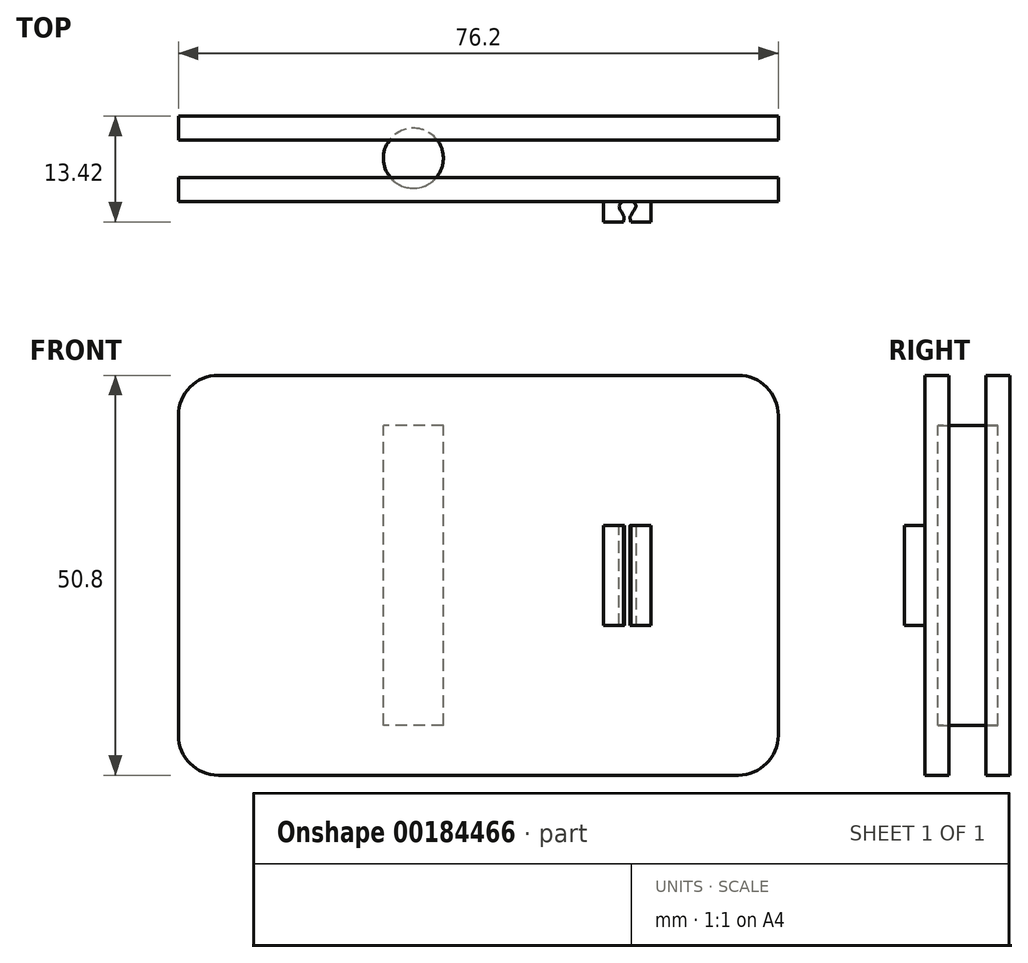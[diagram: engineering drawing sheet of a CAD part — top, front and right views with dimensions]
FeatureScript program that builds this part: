
annotation { "Feature Type Name" : "Feature", "Feature Type Description" : "" }
export const myFeature = defineFeature(function(context is Context, id is Id, definition is map)
    precondition{}
    {
        {
            var Q0;
            Q0=qCreatedBy(makeId("Front.planeOp"),FACE);
            var sketch = newSketch(context, id + "F0", { "sketchPlane" : qUnion([Q0])});
            skLineSegment(sketch, "E0.bottom", {"start": v(38.1, 25.4) * mm, "end": v(-38.1, 25.4) * mm});
            skLineSegment(sketch, "E0.top", {"start": v(38.1, -25.4) * mm, "end": v(-38.1, -25.4) * mm});
            skLineSegment(sketch, "E0.left", {"start": v(38.1, 25.4) * mm, "end": v(38.1, -25.4) * mm});
            skLineSegment(sketch, "E0.right", {"start": v(-38.1, 25.4) * mm, "end": v(-38.1, -25.4) * mm});
            skPoint(sketch, "E0.middle", {"position": v(0, 0) * mm});
            skSolve(sketch);
        }
        {
            var Q0;
            Q0=makeQuery(id+"F0.imprint","IMPRINT",FACE,{"disambiguationData":[TD([[makeQuery(id+"F0.imprint","IMPRINT",EDGE,{"derivedFrom":sQuery(id+"F0.wireOp",EDGE,"E0.bottom")}),1.0]])]});
            extrude(context, id + "F1", {"entities" : qUnion([Q0]), "depth" : 3.05 * mm});
        }
        {
            var Q0;
            Q0=qCreatedBy(makeId("Top.planeOp"),FACE);
            var sketch = newSketch(context, id + "F2", { "sketchPlane" : qUnion([Q0])});
            skPoint(sketch, "E1", {"position": v(-8.25, 2.43) * mm});
            skCircle(sketch, "E2", {"center": v(-8.25, 2.43) * mm, "radius": 3.8 * mm});
            skSolve(sketch);
        }
        {
            var Q0;
            Q0=makeQuery(id+"F2.imprint","IMPRINT",FACE,{"disambiguationData":[TD([[makeQuery(id+"F2.imprint","IMPRINT",EDGE,{"derivedFrom":sQuery(id+"F2.wireOp",EDGE,"E2")}),1.0]])]});
            extrude(context, id + "F3", {"entities" : qUnion([Q0]), "endBound" : BoundingType.SYMMETRIC, "oppositeDirection" : true, "depth" : 38.1 * mm});
        }
        {
            var Q0;
            Q0=qCreatedBy(makeId("Right.planeOp"),FACE);
            var sketch = newSketch(context, id + "F4", { "sketchPlane" : qUnion([Q0])});
            skLineSegment(sketch, "E3.bottom", {"start": v(4.71, -25.4) * mm, "end": v(7.76, -25.4) * mm});
            skLineSegment(sketch, "E3.top", {"start": v(4.71, 25.4) * mm, "end": v(7.76, 25.4) * mm});
            skLineSegment(sketch, "E3.left", {"start": v(4.71, -25.4) * mm, "end": v(4.71, 25.4) * mm});
            skLineSegment(sketch, "E3.right", {"start": v(7.76, -25.4) * mm, "end": v(7.76, 25.4) * mm});
            skPoint(sketch, "E3.middle", {"position": v(6.24, 0) * mm});
            skSolve(sketch);
        }
        {
            var Q0;
            Q0 = qSketchRegion(id + "F4", true);
            extrude(context, id + "F5", {"entities" : qUnion([Q0]), "endBound" : BoundingType.SYMMETRIC, "depth" : 76.2 * mm});
        }
        {
            var Q0;
            Q0=qCreatedBy(makeId("Top.planeOp"),FACE);
            var sketch = newSketch(context, id + "F6", { "sketchPlane" : qUnion([Q0])});
            skPoint(sketch, "E4", {"position": v(15.88, -2.87) * mm});
            skPoint(sketch, "E5", {"position": v(21.94, -2.87) * mm});
            skPoint(sketch, "E6", {"position": v(21.94, -3.6) * mm});
            skPoint(sketch, "E7", {"position": v(15.88, -3.6) * mm});
            skPoint(sketch, "E8", {"position": v(15.88, -4.77) * mm});
            skPoint(sketch, "E9", {"position": v(15.88, -5.66) * mm});
            skPoint(sketch, "E10", {"position": v(21.94, -4.77) * mm});
            skPoint(sketch, "E11", {"position": v(21.94, -5.66) * mm});
            skLineSegment(sketch, "E12", {"start": v(15.88, -5.66) * mm, "end": v(18.42, -5.66) * mm});
            skLineSegment(sketch, "E13", {"start": v(15.88, -5.66) * mm, "end": v(15.88, -2.87) * mm});
            skLineSegment(sketch, "E14", {"start": v(19.4, -5.66) * mm, "end": v(21.94, -5.66) * mm});
            skLineSegment(sketch, "E15", {"start": v(21.94, -2.87) * mm, "end": v(21.94, -5.66) * mm});
            skFitSpline(sketch, "E16", {"points": [v(15.88, -2.87) * mm, v(18.9, -1.91) * mm, v(21.94, -2.87) * mm], "startDerivative": vector(2.6, 1.29) * mm, "endDerivative": vector(2.6, -1.33) * mm});
            skFitSpline(sketch, "E17", {"points": [v(18.42, -5.66) * mm, v(18.42, -4.77) * mm, v(17.9, -3.6) * mm, v(19.05, -2.99) * mm, v(20, -3.6) * mm, v(19.4, -4.77) * mm, v(19.4, -5.66) * mm], "startDerivative": vector(2.47, 8.7) * mm, "endDerivative": vector(2.78, -8.49) * mm});
            skSolve(sketch);
        }
        {
            var Q0;
            Q0=makeQuery(id+"F6.imprint","IMPRINT",FACE,{"disambiguationData":[TD([[makeQuery(id+"F6.imprint","IMPRINT",EDGE,{"derivedFrom":sQuery(id+"F6.wireOp",EDGE,"E12")}),1.0]])]});
            extrude(context, id + "F7", {"entities" : qUnion([Q0]), "operationType" : NewBodyOperationType.ADD, "endBound" : BoundingType.SYMMETRIC, "depth" : 12.7 * mm});
        }
        {
            var Q0;
            Q0=makeQuery(id+"F1.opExtrude","SWEPT_EDGE",EDGE,{"disambiguationData":[OSD([sQuery(id+"F0.wireOp",EDGE,"E0.top"),sQuery(id+"F0.wireOp",EDGE,"E0.left")])]});
            var Q1;
            Q1=makeQuery(id+"F5.opExtrude","CAP_EDGE",EDGE,{"disambiguationData":[OSD([sQuery(id+"F4.wireOp",EDGE,"E3.bottom")])],"isStart":false});
            var Q2;
            Q2=makeQuery(id+"F1.opExtrude","SWEPT_EDGE",EDGE,{"disambiguationData":[OSD([sQuery(id+"F0.wireOp",EDGE,"E0.top"),sQuery(id+"F0.wireOp",EDGE,"E0.right")])]});
            var Q3;
            Q3=makeQuery(id+"F5.opExtrude","CAP_EDGE",EDGE,{"disambiguationData":[OSD([sQuery(id+"F4.wireOp",EDGE,"E3.bottom")])],"isStart":true});
            var Q4;
            Q4=makeQuery(id+"F1.opExtrude","SWEPT_EDGE",EDGE,{"disambiguationData":[OSD([sQuery(id+"F0.wireOp",EDGE,"E0.bottom"),sQuery(id+"F0.wireOp",EDGE,"E0.left")])]});
            var Q5;
            Q5=makeQuery(id+"F5.opExtrude","CAP_EDGE",EDGE,{"disambiguationData":[OSD([sQuery(id+"F4.wireOp",EDGE,"E3.top")])],"isStart":false});
            var Q6;
            Q6=makeQuery(id+"F1.opExtrude","SWEPT_EDGE",EDGE,{"disambiguationData":[OSD([sQuery(id+"F0.wireOp",EDGE,"E0.bottom"),sQuery(id+"F0.wireOp",EDGE,"E0.right")])]});
            var Q7;
            Q7=makeQuery(id+"F5.opExtrude","CAP_EDGE",EDGE,{"disambiguationData":[OSD([sQuery(id+"F4.wireOp",EDGE,"E3.top")])],"isStart":true});
            fillet(context, id + "F8", {"entities" : qUnion([Q0, Q1, Q2, Q3, Q4, Q5, Q6, Q7]), "radius" : 5.08 * mm, "tangentPropagation" : true, "allowEdgeOverflow" : false});
        }
    });
